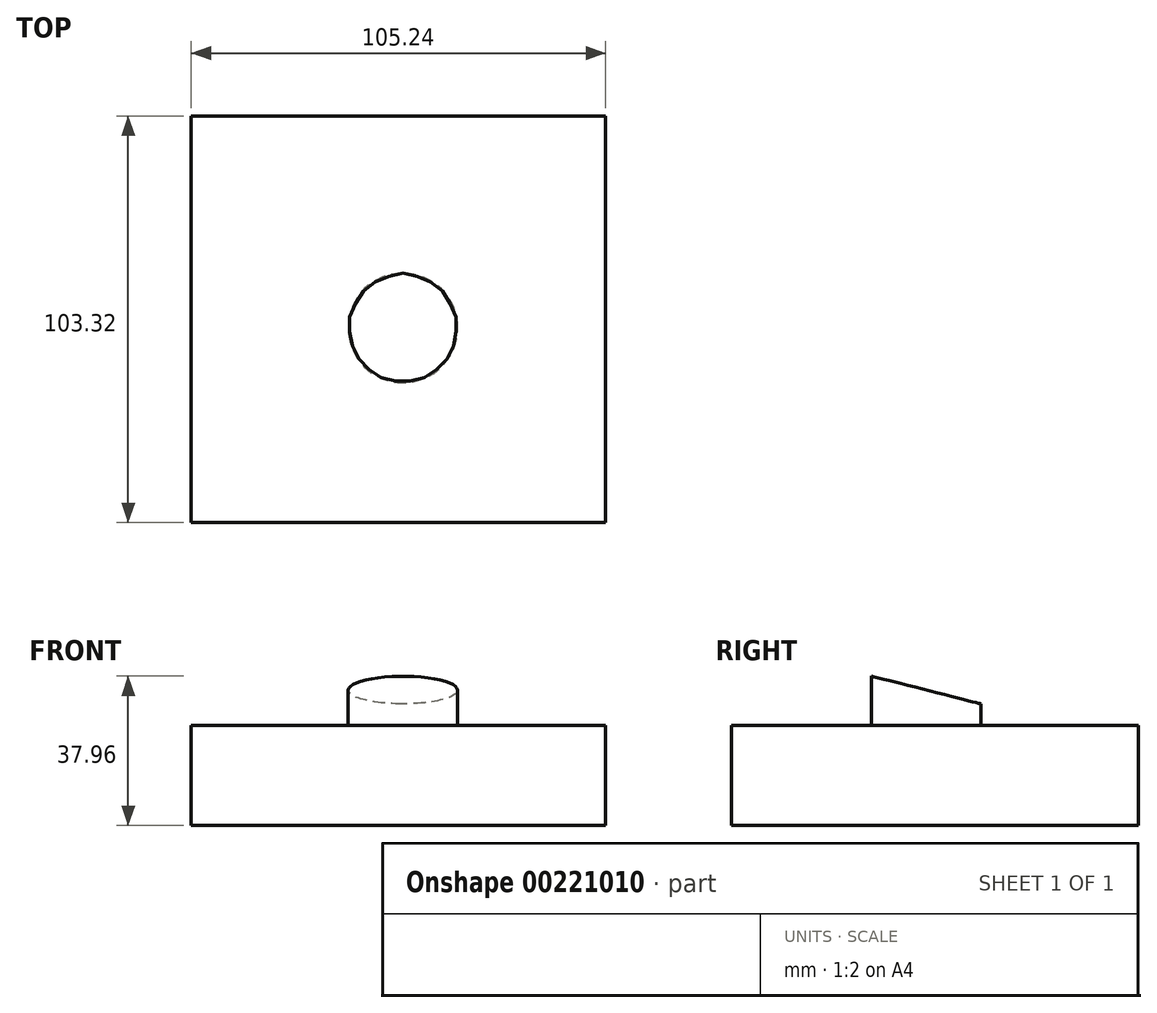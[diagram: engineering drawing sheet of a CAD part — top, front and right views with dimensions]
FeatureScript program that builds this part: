
annotation { "Feature Type Name" : "Feature", "Feature Type Description" : "" }
export const myFeature = defineFeature(function(context is Context, id is Id, definition is map)
    precondition{}
    {
        {
            var Q0;
            Q0=qCreatedBy(makeId("Top.planeOp"),FACE);
            var sketch = newSketch(context, id + "F0", { "sketchPlane" : qUnion([Q0])});
            skLineSegment(sketch, "E0.bottom", {"start": v(-53.77, 53.86) * mm, "end": v(51.47, 53.86) * mm});
            skLineSegment(sketch, "E0.top", {"start": v(-53.77, -49.46) * mm, "end": v(51.47, -49.46) * mm});
            skLineSegment(sketch, "E0.left", {"start": v(-53.77, 53.86) * mm, "end": v(-53.77, -49.46) * mm});
            skLineSegment(sketch, "E0.right", {"start": v(51.47, 53.86) * mm, "end": v(51.47, -49.46) * mm});
            skSolve(sketch);
        }
        {
            var Q0;
            Q0 = qSketchRegion(id + "F0", true);
            extrude(context, id + "F1", {"entities" : qUnion([Q0]), "depth" : 25.4 * mm});
        }
        {
            var Q0;
            Q0=makeQuery(id+"F1.opExtrude","CAP_FACE",FACE,{"disambiguationData":[OSD([sQuery(id+"F0.wireOp",EDGE,"E0.bottom"),sQuery(id+"F0.wireOp",EDGE,"E0.top"),sQuery(id+"F0.wireOp",EDGE,"E0.left"),sQuery(id+"F0.wireOp",EDGE,"E0.right")])],"isStart":false});
            var sketch = newSketch(context, id + "F2", { "sketchPlane" : qUnion([Q0])});
            skCircle(sketch, "E1", {"center": v(0, 0) * mm, "radius": 13.9 * mm});
            skSolve(sketch);
        }
        {
            var Q0;
            Q0 = qSketchRegion(id + "F2", true);
            extrude(context, id + "F3", {"entities" : qUnion([Q0]), "operationType" : NewBodyOperationType.ADD, "depth" : 12.7 * mm});
        }
        {
            var Q0;
            Q0=makeQuery(id+"F1.opExtrude","SWEPT_FACE",FACE,{"disambiguationData":[OSD([sQuery(id+"F0.wireOp",EDGE,"E0.right")])]});
            var sketch = newSketch(context, id + "F4", { "sketchPlane" : qUnion([Q0])});
            skLineSegment(sketch, "E2", {"start": v(-17.78, 38.95) * mm, "end": v(20.9, 38.95) * mm});
            skLineSegment(sketch, "E3", {"start": v(20.9, 38.95) * mm, "end": v(20.9, 29.14) * mm});
            skLineSegment(sketch, "E4", {"start": v(20.9, 29.14) * mm, "end": v(-17.78, 38.95) * mm});
            skSolve(sketch);
        }
        {
            var Q0;
            Q0 = qSketchRegion(id + "F4", true);
            extrude(context, id + "F5", {"entities" : qUnion([Q0]), "operationType" : NewBodyOperationType.REMOVE, "endBound" : BoundingType.THROUGH_ALL, "oppositeDirection" : true, "depth" : 25.4 * mm});
        }
    });
